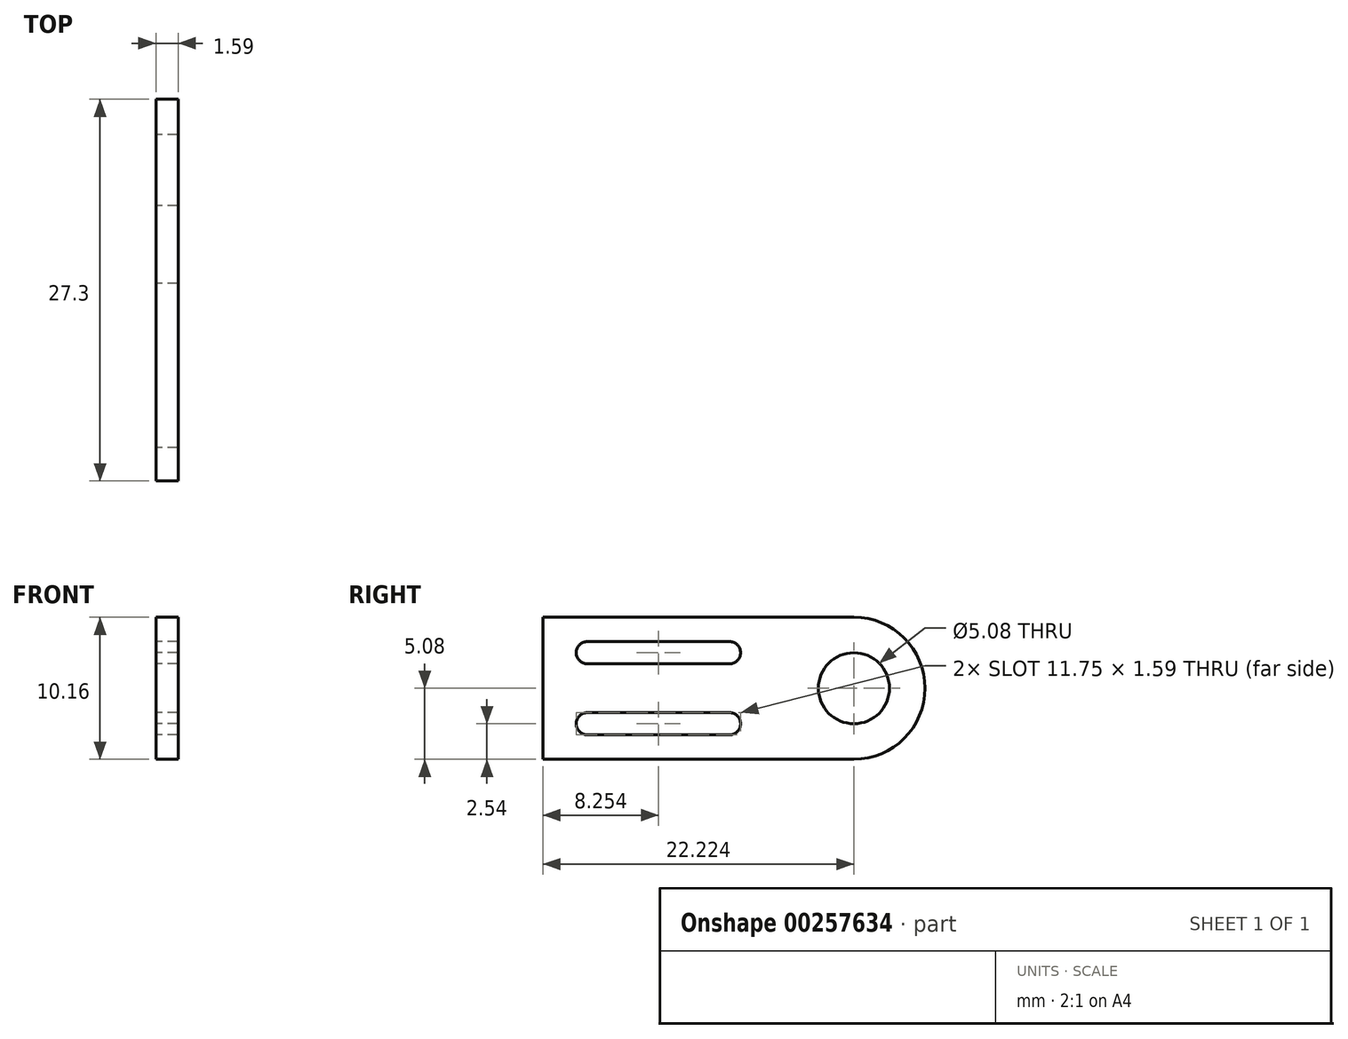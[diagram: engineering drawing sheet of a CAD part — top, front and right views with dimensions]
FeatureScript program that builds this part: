
annotation { "Feature Type Name" : "Feature", "Feature Type Description" : "" }
export const myFeature = defineFeature(function(context is Context, id is Id, definition is map)
    precondition{}
    {
        {
            var Q0;
            Q0=qCreatedBy(makeId("Right.planeOp"),FACE);
            var sketch = newSketch(context, id + "F0", { "sketchPlane" : qUnion([Q0])});
            skLineSegment(sketch, "E0.bottom", {"start": v(-12.01, 5.08) * mm, "end": v(10.21, 5.08) * mm});
            skLineSegment(sketch, "E0.top", {"start": v(-12.01, -5.08) * mm, "end": v(10.21, -5.08) * mm});
            skLineSegment(sketch, "E0.left", {"start": v(-12.01, 5.08) * mm, "end": v(-12.01, -5.08) * mm});
            skLineSegment(sketch, "E1", {"start": v(-9.17, 0) * mm, "end": v(12, 0) * mm, "construction": true});
            skLineSegment(sketch, "E2", {"start": v(0, -7.22) * mm, "end": v(0, 6.64) * mm, "construction": true});
            skLineSegment(sketch, "E3", {"start": v(10.21, -6.25) * mm, "end": v(10.21, 6.6) * mm, "construction": true});
            skCircle(sketch, "E4", {"center": v(10.21, 0) * mm, "radius": 2.54 * mm});
            skLineSegment(sketch, "E5", {"start": v(-10.01, 2.54) * mm, "end": v(4.53, 2.54) * mm, "construction": true});
            skLineSegment(sketch, "E6", {"start": v(-9.97, -2.54) * mm, "end": v(4.34, -2.54) * mm, "construction": true});
            skCircle(sketch, "E7", {"center": v(-8.84, 2.54) * mm, "radius": 0.8 * mm});
            skCircle(sketch, "E8", {"center": v(1.32, 2.54) * mm, "radius": 0.8 * mm});
            skCircle(sketch, "E9", {"center": v(-8.84, -2.54) * mm, "radius": 0.8 * mm});
            skCircle(sketch, "E10", {"center": v(1.32, -2.54) * mm, "radius": 0.8 * mm});
            skLineSegment(sketch, "E11.bottom", {"start": v(-8.84, 3.33) * mm, "end": v(1.32, 3.33) * mm});
            skLineSegment(sketch, "E11.top", {"start": v(-8.84, 1.75) * mm, "end": v(1.32, 1.75) * mm});
            skLineSegment(sketch, "E11.left", {"start": v(-8.84, 3.33) * mm, "end": v(-8.84, 1.75) * mm});
            skLineSegment(sketch, "E11.right", {"start": v(1.32, 3.33) * mm, "end": v(1.32, 1.75) * mm});
            skLineSegment(sketch, "E12.bottom", {"start": v(-8.84, -1.75) * mm, "end": v(1.32, -1.75) * mm});
            skLineSegment(sketch, "E12.top", {"start": v(-8.84, -3.33) * mm, "end": v(1.32, -3.33) * mm});
            skLineSegment(sketch, "E12.left", {"start": v(-8.84, -1.75) * mm, "end": v(-8.84, -3.33) * mm});
            skLineSegment(sketch, "E12.right", {"start": v(1.32, -1.75) * mm, "end": v(1.32, -3.33) * mm});
            skCircle(sketch, "E13", {"center": v(10.21, 0) * mm, "radius": 5.08 * mm});
            skSolve(sketch);
        }
        {
            var Q0;
            Q0 = qSketchRegion(id + "F0", true);
            extrude(context, id + "F1", {"entities" : qUnion([Q0]), "depth" : 1.59 * mm});
        }
    });
